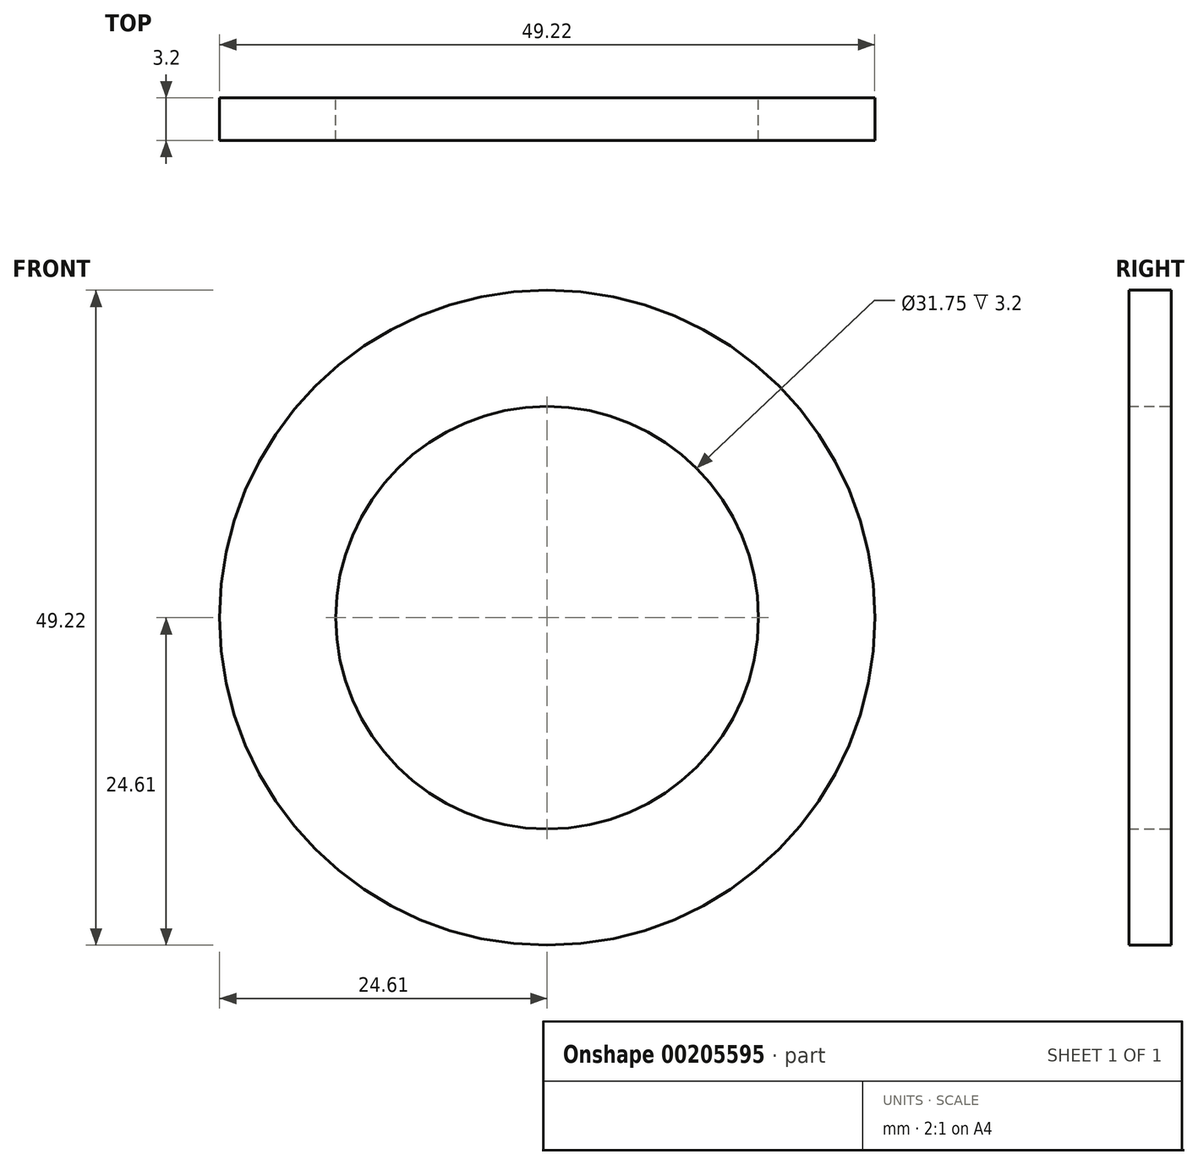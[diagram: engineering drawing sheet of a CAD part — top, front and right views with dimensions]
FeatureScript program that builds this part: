
annotation { "Feature Type Name" : "Feature", "Feature Type Description" : "" }
export const myFeature = defineFeature(function(context is Context, id is Id, definition is map)
    precondition{}
    {
        {
            var Q0;
            Q0=qCreatedBy(makeId("Front.planeOp"),FACE);
            var sketch = newSketch(context, id + "F0", { "sketchPlane" : qUnion([Q0])});
            skCircle(sketch, "E0", {"center": v(0, 0) * mm, "radius": 15.88 * mm});
            skCircle(sketch, "E1", {"center": v(0, 0) * mm, "radius": 24.61 * mm});
            skSolve(sketch);
        }
        {
            var Q0;
            Q0=qSketchRegion(id+"F0",true);
            extrude(context, id + "F1", {"entities" : qUnion([Q0]), "depth" : 3.2 * mm});
        }
    });
